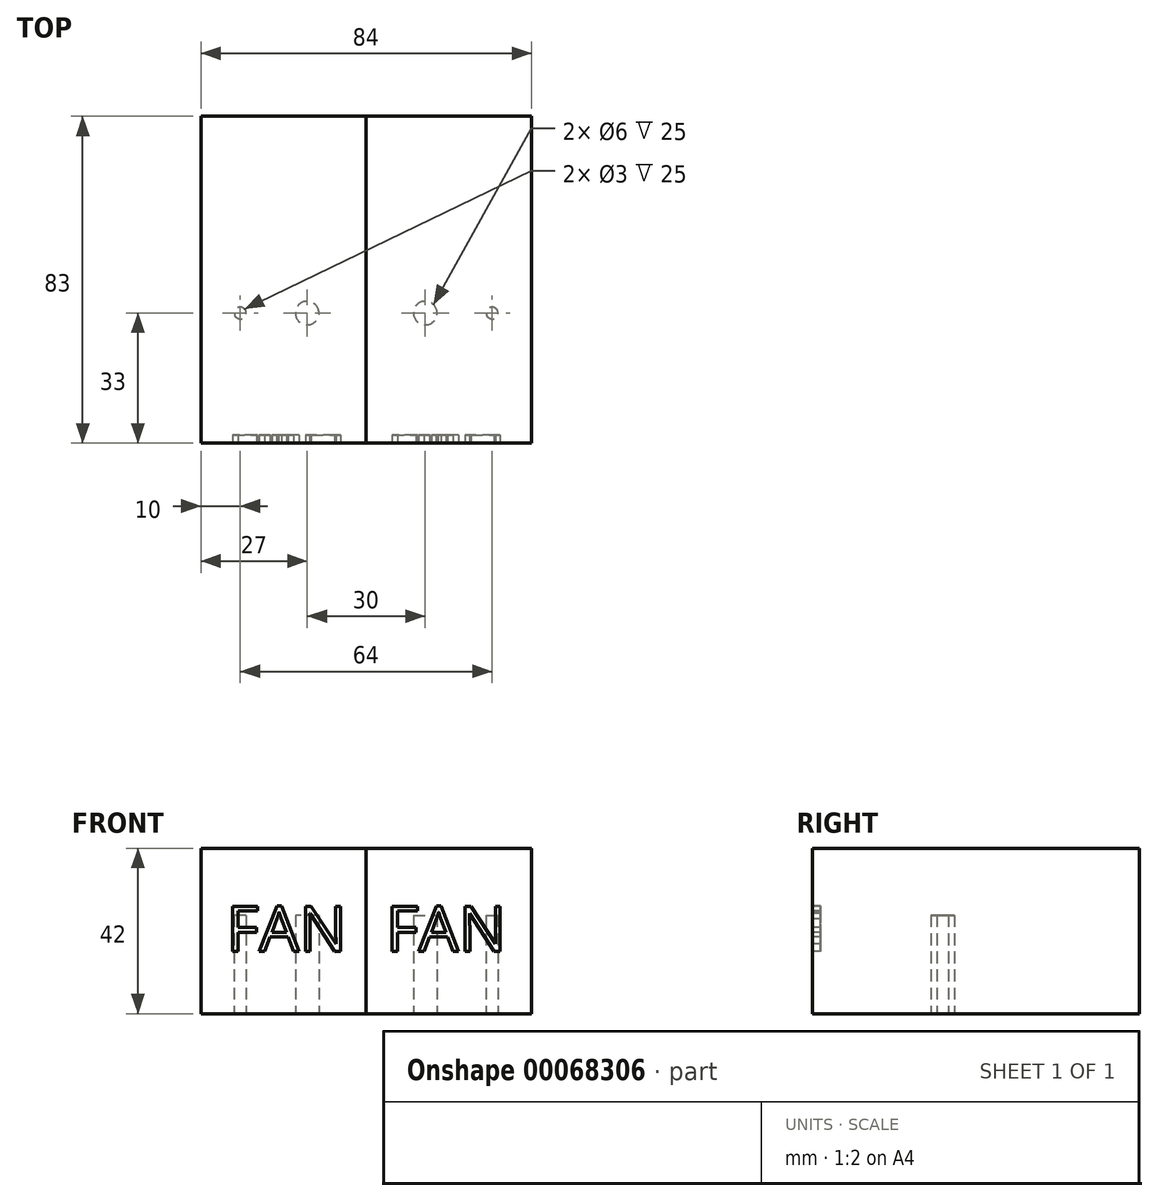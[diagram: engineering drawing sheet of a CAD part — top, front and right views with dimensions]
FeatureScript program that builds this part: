
annotation { "Feature Type Name" : "Feature", "Feature Type Description" : "" }
export const myFeature = defineFeature(function(context is Context, id is Id, definition is map)
    precondition{}
    {
        {
            var Q0;
            Q0=qCreatedBy(makeId("Front.planeOp"),FACE);
            var sketch = newSketch(context, id + "F0", { "sketchPlane" : qUnion([Q0])});
            skLineSegment(sketch, "E0.bottom", {"start": v(0, 42) * mm, "end": v(42, 42) * mm});
            skLineSegment(sketch, "E0.top", {"start": v(0, 0) * mm, "end": v(42, 0) * mm});
            skLineSegment(sketch, "E0.left", {"start": v(0, 42) * mm, "end": v(0, 0) * mm});
            skLineSegment(sketch, "E0.right", {"start": v(42, 42) * mm, "end": v(42, 0) * mm});
            skSolve(sketch);
        }
        {
            var Q0;
            Q0 = qSketchRegion(id + "F0", true);
            extrude(context, id + "F1", {"entities" : qUnion([Q0]), "depth" : 83 * mm});
        }
        {
            var Q0;
            Q0=makeQuery(id+"F1.opExtrude","SWEPT_FACE",FACE,{"disambiguationData":[OSD([sQuery(id+"F0.wireOp",EDGE,"E0.top")])]});
            var sketch = newSketch(context, id + "F2", { "sketchPlane" : qUnion([Q0])});
            skCircle(sketch, "E1", {"center": v(32, 50) * mm, "radius": 1.5 * mm});
            skCircle(sketch, "E2", {"center": v(15, 50) * mm, "radius": 3 * mm});
            skSolve(sketch);
        }
        {
            var Q0;
            Q0 = qSketchRegion(id + "F2", true);
            extrude(context, id + "F3", {"entities" : qUnion([Q0]), "operationType" : NewBodyOperationType.REMOVE, "oppositeDirection" : true, "depth" : 25 * mm});
        }
        {
            var Q0;
            Q0=makeQuery(id+"F1.opExtrude","SWEPT_BODY",BODY,{"disambiguationData":[OSD([sQuery(id+"F0.wireOp",EDGE,"E0.bottom"),sQuery(id+"F0.wireOp",EDGE,"E0.top"),sQuery(id+"F0.wireOp",EDGE,"E0.left"),sQuery(id+"F0.wireOp",EDGE,"E0.right")])]});
            var Q1;
            Q1=qCreatedBy(makeId("Right.planeOp"),FACE);
            mirror(context, id + "F4", {"entities" : qUnion([Q0]), "mirrorPlane" : qUnion([Q1])});
        }
        {
            var Q0;
            Q0=makeQuery(id+"F1.opExtrude","CAP_FACE",FACE,{"disambiguationData":[OSD([sQuery(id+"F0.wireOp",EDGE,"E0.bottom"),sQuery(id+"F0.wireOp",EDGE,"E0.top"),sQuery(id+"F0.wireOp",EDGE,"E0.left"),sQuery(id+"F0.wireOp",EDGE,"E0.right")])],"isStart":false});
            var sketch = newSketch(context, id + "F5", { "sketchPlane" : qUnion([Q0])});
            skText(sketch, "E3", { "text": "FAN", "fontName": "OpenSans-Regular.ttf"});
            const initialGuessF5  = {"E3": [0.00503, 0.0158, 1, 0, 0.01158]};
            skSetInitialGuess(sketch, initialGuessF5);
            skSolve(sketch);
        }
        {
            var Q0;
            Q0 = qSketchRegion(id + "F5", true);
            extrude(context, id + "F6", {"entities" : qUnion([Q0]), "operationType" : NewBodyOperationType.REMOVE, "oppositeDirection" : true, "depth" : 2 * mm});
        }
        {
            var Q0;
            Q0=makeQuery(id+"F4.opPattern","COPY",FACE,{"derivedFrom":makeQuery(id+"F1.opExtrude","CAP_FACE",FACE,{"disambiguationData":[OSD([sQuery(id+"F0.wireOp",EDGE,"E0.bottom"),sQuery(id+"F0.wireOp",EDGE,"E0.top"),sQuery(id+"F0.wireOp",EDGE,"E0.left"),sQuery(id+"F0.wireOp",EDGE,"E0.right")])],"isStart":false}),"instanceName":"1"});
            var sketch = newSketch(context, id + "F7", { "sketchPlane" : qUnion([Q0])});
            skText(sketch, "E4", { "text": "FAN", "fontName": "OpenSans-Regular.ttf"});
            skLineSegment(sketch, "E5", {"start": v(-21, 0) * mm, "end": v(-21, 15.8) * mm});
            const initialGuessF7  = {"E4": [-0.03551, 0.0158, 1, 0, 0.01158]};
            skSetInitialGuess(sketch, initialGuessF7);
            skSolve(sketch);
        }
        {
            var Q0;
            Q0 = qSketchRegion(id + "F7", true);
            extrude(context, id + "F8", {"entities" : qUnion([Q0]), "operationType" : NewBodyOperationType.REMOVE, "oppositeDirection" : true, "depth" : 2 * mm});
        }
    });
